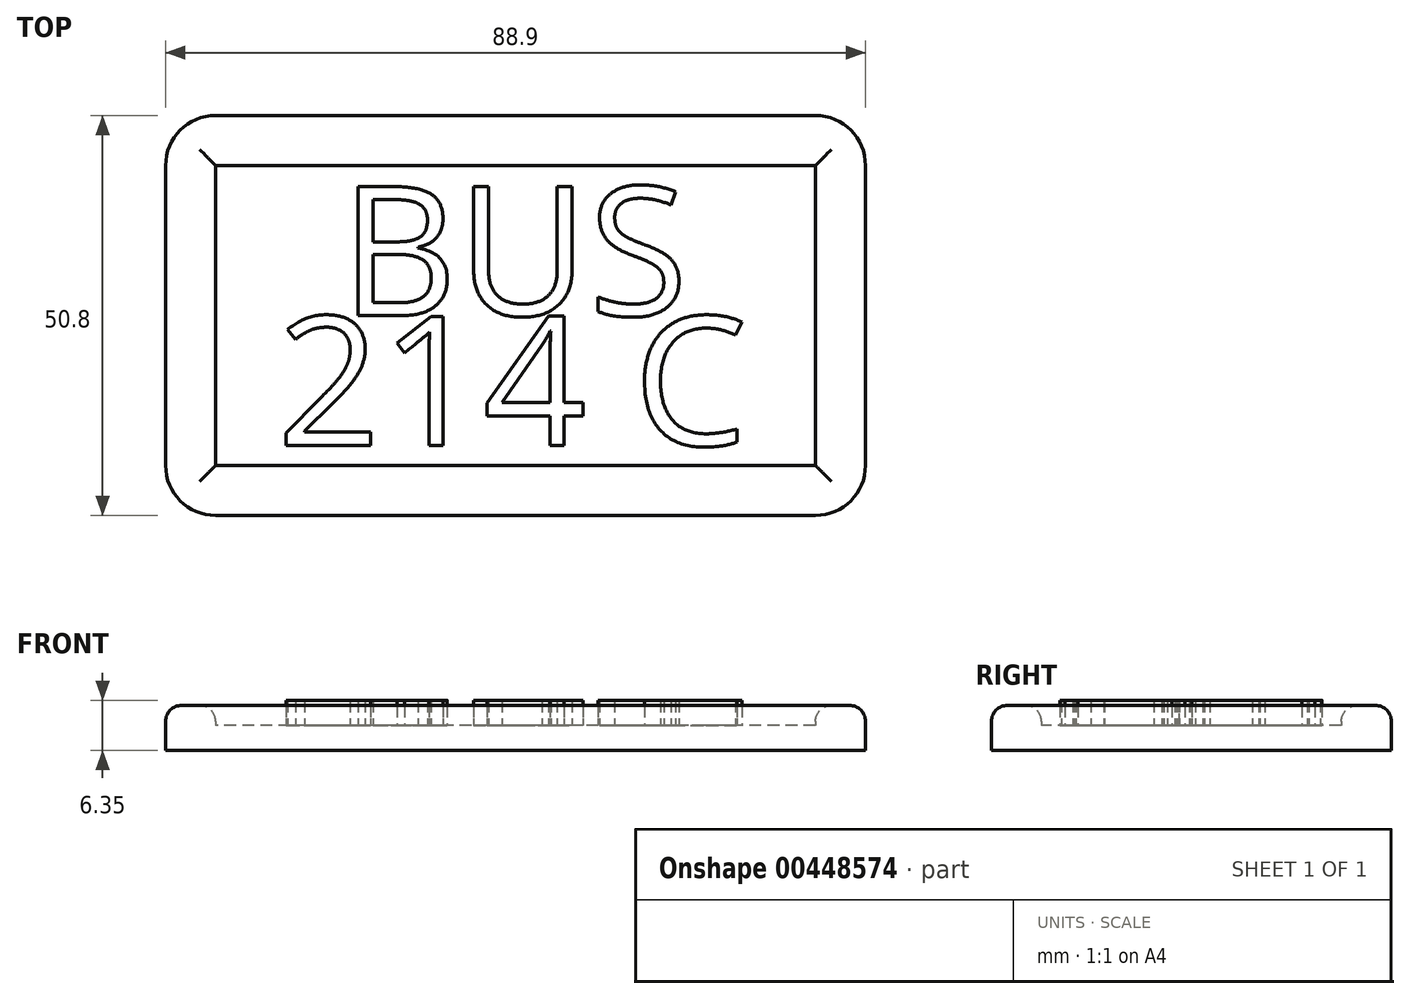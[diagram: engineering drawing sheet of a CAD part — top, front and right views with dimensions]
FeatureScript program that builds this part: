
annotation { "Feature Type Name" : "Feature", "Feature Type Description" : "" }
export const myFeature = defineFeature(function(context is Context, id is Id, definition is map)
    precondition{}
    {
        {
            var Q0;
            Q0=qCreatedBy(makeId("Top.planeOp"),FACE);
            var sketch = newSketch(context, id + "F0", { "sketchPlane" : qUnion([Q0])});
            skLineSegment(sketch, "E0.bottom", {"start": v(38.1, 25.4) * mm, "end": v(-38.1, 25.4) * mm});
            skLineSegment(sketch, "E0.top", {"start": v(38.1, -25.4) * mm, "end": v(-38.1, -25.4) * mm});
            skLineSegment(sketch, "E0.left", {"start": v(44.45, 19.05) * mm, "end": v(44.45, -19.05) * mm});
            skLineSegment(sketch, "E0.right", {"start": v(-44.45, 19.05) * mm, "end": v(-44.45, -19.05) * mm});
            skPoint(sketch, "E0.middle", {"position": v(0, 0) * mm});
            skPoint(sketch, "E1.visualSharp", {"position": v(-44.45, 25.4) * mm});
            skArc(sketch, "E1.filletArc", {"start": v(-38.1, 25.4) * mm, "mid": v(-42.6, 23.54) * mm, "end": v(-44.45, 19.05) * mm});
            skPoint(sketch, "E2.visualSharp", {"position": v(44.45, 25.4) * mm});
            skArc(sketch, "E2.filletArc", {"start": v(44.45, 19.05) * mm, "mid": v(42.6, 23.54) * mm, "end": v(38.1, 25.4) * mm});
            skPoint(sketch, "E3.visualSharp", {"position": v(44.45, -25.4) * mm});
            skArc(sketch, "E3.filletArc", {"start": v(38.1, -25.4) * mm, "mid": v(42.6, -23.54) * mm, "end": v(44.45, -19.05) * mm});
            skPoint(sketch, "E4.visualSharp", {"position": v(-44.45, -25.4) * mm});
            skArc(sketch, "E4.filletArc", {"start": v(-44.45, -19.05) * mm, "mid": v(-42.6, -23.54) * mm, "end": v(-38.1, -25.4) * mm});
            skLineSegment(sketch, "E5.0", {"start": v(38.1, 19.05) * mm, "end": v(38.1, -19.05) * mm});
            skLineSegment(sketch, "E5.1", {"start": v(38.1, -19.05) * mm, "end": v(38.1, -19.05) * mm});
            skLineSegment(sketch, "E5.2", {"start": v(38.1, 19.05) * mm, "end": v(38.1, 19.05) * mm});
            skLineSegment(sketch, "E5.3", {"start": v(38.1, -19.05) * mm, "end": v(-38.1, -19.05) * mm});
            skLineSegment(sketch, "E5.4", {"start": v(38.1, 19.05) * mm, "end": v(-38.1, 19.05) * mm});
            skLineSegment(sketch, "E5.5", {"start": v(-38.1, 19.05) * mm, "end": v(-38.1, 19.05) * mm});
            skLineSegment(sketch, "E5.6", {"start": v(-38.1, 19.05) * mm, "end": v(-38.1, -19.05) * mm});
            skLineSegment(sketch, "E5.7", {"start": v(-38.1, -19.05) * mm, "end": v(-38.1, -19.05) * mm});
            skLineSegment(sketch, "E6.0", {"start": v(44.45, 16.5) * mm, "end": v(-44.45, 16.5) * mm, "construction": true});
            skText(sketch, "E7", { "text": "BUS", "fontName": "OpenSans-Regular.ttf"});
            skLineSegment(sketch, "E8.0", {"start": v(44.45, -16.5) * mm, "end": v(-44.45, -16.5) * mm, "construction": true});
            skText(sketch, "E9", { "text": "214 C", "fontName": "OpenSans-Regular.ttf"});
            const initialGuessF0  = {"E7": [-0.02226, 0, 1, 0, 0.0165], "E9": [-0.03028, -0.0165, 1, 0, 0.0165]};
            skSetInitialGuess(sketch, initialGuessF0);
            skSolve(sketch);
        }
        {
            var Q0;
            Q0=makeQuery(id+"F0.imprint","IMPRINT",FACE,{"disambiguationData":[TD([[makeQuery(id+"F0.imprint","IMPRINT",EDGE,{"derivedFrom":sQuery(id+"F0.wireOp",EDGE,"E0.bottom")}),1.0]])]});
            extrude(context, id + "F1", {"entities" : qUnion([Q0]), "depth" : 5.7 * mm, "offsetDistance" : 25.4 * mm});
        }
        {
            var Q0;
            Q0=makeQuery(id+"F0.imprint","IMPRINT",FACE,{"disambiguationData":[TD([[makeQuery(id+"F0.imprint","IMPRINT",EDGE,{"derivedFrom":sQuery(id+"F0.wireOp",EDGE,"E5.0")}),-1.0]])]});
            extrude(context, id + "F2", {"entities" : qUnion([Q0]), "operationType" : NewBodyOperationType.ADD, "depth" : 3.17 * mm, "offsetDistance" : 25.4 * mm});
        }
        {
            var Q0;
            {var subQ1=sQuery(id+"F0.wireOp",EDGE,"E7.sketch_text.stroke-0");Q0=makeQuery(id+"F0.imprint","IMPRINT",FACE,{"disambiguationData":[TD([[makeQuery(id+"F0.imprint","IMPRINT",EDGE,{"derivedFrom":subQ1}),-1.0]])]});}
            var Q1;
            Q1=makeQuery(id+"F0.imprint","IMPRINT",FACE,{"disambiguationData":[TD([[makeQuery(id+"F0.imprint","IMPRINT",EDGE,{"derivedFrom":sQuery(id+"F0.wireOp",EDGE,"E7.sketch_text.stroke-25")}),-1.0]])]});
            var Q2;
            Q2=makeQuery(id+"F0.imprint","IMPRINT",FACE,{"disambiguationData":[TD([[makeQuery(id+"F0.imprint","IMPRINT",EDGE,{"derivedFrom":sQuery(id+"F0.wireOp",EDGE,"E7.sketch_text.stroke-39")}),-1.0]])]});
            var Q3;
            Q3=makeQuery(id+"F0.imprint","IMPRINT",FACE,{"disambiguationData":[TD([[makeQuery(id+"F0.imprint","IMPRINT",EDGE,{"derivedFrom":sQuery(id+"F0.wireOp",EDGE,"E9.sketch_text.stroke-46")}),-1.0]])]});
            var Q4;
            Q4=makeQuery(id+"F0.imprint","IMPRINT",FACE,{"disambiguationData":[TD([[makeQuery(id+"F0.imprint","IMPRINT",EDGE,{"derivedFrom":sQuery(id+"F0.wireOp",EDGE,"E9.sketch_text.stroke-29")}),-1.0]])]});
            var Q5;
            Q5=makeQuery(id+"F0.imprint","IMPRINT",FACE,{"disambiguationData":[TD([[makeQuery(id+"F0.imprint","IMPRINT",EDGE,{"derivedFrom":sQuery(id+"F0.wireOp",EDGE,"E9.sketch_text.stroke-20")}),-1.0]])]});
            var Q6;
            Q6=makeQuery(id+"F0.imprint","IMPRINT",FACE,{"disambiguationData":[TD([[makeQuery(id+"F0.imprint","IMPRINT",EDGE,{"derivedFrom":sQuery(id+"F0.wireOp",EDGE,"E9.sketch_text.stroke-0")}),-1.0]])]});
            extrude(context, id + "F3", {"entities" : qUnion([Q0, Q1, Q2, Q3, Q4, Q5, Q6]), "operationType" : NewBodyOperationType.ADD, "depth" : 6.35 * mm, "offsetDistance" : 25.4 * mm});
        }
        {
            var Q0;
            Q0=makeQuery(id+"F0.imprint","IMPRINT",FACE,{"disambiguationData":[TD([[makeQuery(id+"F0.imprint","IMPRINT",EDGE,{"derivedFrom":sQuery(id+"F0.wireOp",EDGE,"E9.sketch_text.stroke-40")}),1.0]])]});
            var Q1;
            Q1=makeQuery(id+"F0.imprint","IMPRINT",FACE,{"disambiguationData":[TD([[makeQuery(id+"F0.imprint","IMPRINT",EDGE,{"derivedFrom":sQuery(id+"F0.wireOp",EDGE,"E7.sketch_text.stroke-18")}),1.0]])]});
            var Q2;
            Q2=makeQuery(id+"F0.imprint","IMPRINT",FACE,{"disambiguationData":[TD([[makeQuery(id+"F0.imprint","IMPRINT",EDGE,{"derivedFrom":sQuery(id+"F0.wireOp",EDGE,"E7.sketch_text.stroke-11")}),1.0]])]});
            var Q3;
            Q3=makeQuery(id+"F2.opExtrude","CAP_FACE",FACE,{"disambiguationData":[OSD([sQuery(id+"F0.wireOp",EDGE,"E5.0"),sQuery(id+"F0.wireOp",EDGE,"E5.3"),sQuery(id+"F0.wireOp",EDGE,"E5.4"),sQuery(id+"F0.wireOp",EDGE,"E5.6"),sQuery(id+"F0.wireOp",EDGE,"E7.sketch_text.stroke-0"),sQuery(id+"F0.wireOp",EDGE,"E7.sketch_text.stroke-1"),sQuery(id+"F0.wireOp",EDGE,"E7.sketch_text.stroke-2"),sQuery(id+"F0.wireOp",EDGE,"E7.sketch_text.stroke-3"),sQuery(id+"F0.wireOp",EDGE,"E7.sketch_text.stroke-4"),sQuery(id+"F0.wireOp",EDGE,"E7.sketch_text.stroke-5"),sQuery(id+"F0.wireOp",EDGE,"E7.sketch_text.stroke-6"),sQuery(id+"F0.wireOp",EDGE,"E7.sketch_text.stroke-7"),sQuery(id+"F0.wireOp",EDGE,"E7.sketch_text.stroke-8"),sQuery(id+"F0.wireOp",EDGE,"E7.sketch_text.stroke-9"),sQuery(id+"F0.wireOp",EDGE,"E7.sketch_text.stroke-10"),sQuery(id+"F0.wireOp",EDGE,"E7.sketch_text.stroke-25"),sQuery(id+"F0.wireOp",EDGE,"E7.sketch_text.stroke-26"),sQuery(id+"F0.wireOp",EDGE,"E7.sketch_text.stroke-27"),sQuery(id+"F0.wireOp",EDGE,"E7.sketch_text.stroke-28"),sQuery(id+"F0.wireOp",EDGE,"E7.sketch_text.stroke-29"),sQuery(id+"F0.wireOp",EDGE,"E7.sketch_text.stroke-30"),sQuery(id+"F0.wireOp",EDGE,"E7.sketch_text.stroke-31"),sQuery(id+"F0.wireOp",EDGE,"E7.sketch_text.stroke-32"),sQuery(id+"F0.wireOp",EDGE,"E7.sketch_text.stroke-33"),sQuery(id+"F0.wireOp",EDGE,"E7.sketch_text.stroke-34"),sQuery(id+"F0.wireOp",EDGE,"E7.sketch_text.stroke-35"),sQuery(id+"F0.wireOp",EDGE,"E7.sketch_text.stroke-36"),sQuery(id+"F0.wireOp",EDGE,"E7.sketch_text.stroke-37"),sQuery(id+"F0.wireOp",EDGE,"E7.sketch_text.stroke-38"),sQuery(id+"F0.wireOp",EDGE,"E7.sketch_text.stroke-39"),sQuery(id+"F0.wireOp",EDGE,"E7.sketch_text.stroke-40"),sQuery(id+"F0.wireOp",EDGE,"E7.sketch_text.stroke-41"),sQuery(id+"F0.wireOp",EDGE,"E7.sketch_text.stroke-42"),sQuery(id+"F0.wireOp",EDGE,"E7.sketch_text.stroke-43"),sQuery(id+"F0.wireOp",EDGE,"E7.sketch_text.stroke-44"),sQuery(id+"F0.wireOp",EDGE,"E7.sketch_text.stroke-45"),sQuery(id+"F0.wireOp",EDGE,"E7.sketch_text.stroke-46"),sQuery(id+"F0.wireOp",EDGE,"E7.sketch_text.stroke-47"),sQuery(id+"F0.wireOp",EDGE,"E7.sketch_text.stroke-48"),sQuery(id+"F0.wireOp",EDGE,"E7.sketch_text.stroke-49"),sQuery(id+"F0.wireOp",EDGE,"E7.sketch_text.stroke-50"),sQuery(id+"F0.wireOp",EDGE,"E7.sketch_text.stroke-51"),sQuery(id+"F0.wireOp",EDGE,"E7.sketch_text.stroke-52"),sQuery(id+"F0.wireOp",EDGE,"E7.sketch_text.stroke-53"),sQuery(id+"F0.wireOp",EDGE,"E7.sketch_text.stroke-54"),sQuery(id+"F0.wireOp",EDGE,"E7.sketch_text.stroke-55"),sQuery(id+"F0.wireOp",EDGE,"E7.sketch_text.stroke-56"),sQuery(id+"F0.wireOp",EDGE,"E7.sketch_text.stroke-57"),sQuery(id+"F0.wireOp",EDGE,"E7.sketch_text.stroke-58"),sQuery(id+"F0.wireOp",EDGE,"E7.sketch_text.stroke-59"),sQuery(id+"F0.wireOp",EDGE,"E7.sketch_text.stroke-60"),sQuery(id+"F0.wireOp",EDGE,"E7.sketch_text.stroke-61"),sQuery(id+"F0.wireOp",EDGE,"E7.sketch_text.stroke-62"),sQuery(id+"F0.wireOp",EDGE,"E7.sketch_text.stroke-63"),sQuery(id+"F0.wireOp",EDGE,"E9.sketch_text.stroke-0"),sQuery(id+"F0.wireOp",EDGE,"E9.sketch_text.stroke-1"),sQuery(id+"F0.wireOp",EDGE,"E9.sketch_text.stroke-2"),sQuery(id+"F0.wireOp",EDGE,"E9.sketch_text.stroke-3"),sQuery(id+"F0.wireOp",EDGE,"E9.sketch_text.stroke-4"),sQuery(id+"F0.wireOp",EDGE,"E9.sketch_text.stroke-5"),sQuery(id+"F0.wireOp",EDGE,"E9.sketch_text.stroke-6"),sQuery(id+"F0.wireOp",EDGE,"E9.sketch_text.stroke-7"),sQuery(id+"F0.wireOp",EDGE,"E9.sketch_text.stroke-8"),sQuery(id+"F0.wireOp",EDGE,"E9.sketch_text.stroke-9"),sQuery(id+"F0.wireOp",EDGE,"E9.sketch_text.stroke-10"),sQuery(id+"F0.wireOp",EDGE,"E9.sketch_text.stroke-11"),sQuery(id+"F0.wireOp",EDGE,"E9.sketch_text.stroke-12"),sQuery(id+"F0.wireOp",EDGE,"E9.sketch_text.stroke-13"),sQuery(id+"F0.wireOp",EDGE,"E9.sketch_text.stroke-14"),sQuery(id+"F0.wireOp",EDGE,"E9.sketch_text.stroke-15"),sQuery(id+"F0.wireOp",EDGE,"E9.sketch_text.stroke-16"),sQuery(id+"F0.wireOp",EDGE,"E9.sketch_text.stroke-17"),sQuery(id+"F0.wireOp",EDGE,"E9.sketch_text.stroke-18"),sQuery(id+"F0.wireOp",EDGE,"E9.sketch_text.stroke-19"),sQuery(id+"F0.wireOp",EDGE,"E9.sketch_text.stroke-20"),sQuery(id+"F0.wireOp",EDGE,"E9.sketch_text.stroke-21"),sQuery(id+"F0.wireOp",EDGE,"E9.sketch_text.stroke-22"),sQuery(id+"F0.wireOp",EDGE,"E9.sketch_text.stroke-23"),sQuery(id+"F0.wireOp",EDGE,"E9.sketch_text.stroke-24"),sQuery(id+"F0.wireOp",EDGE,"E9.sketch_text.stroke-25"),sQuery(id+"F0.wireOp",EDGE,"E9.sketch_text.stroke-26"),sQuery(id+"F0.wireOp",EDGE,"E9.sketch_text.stroke-27"),sQuery(id+"F0.wireOp",EDGE,"E9.sketch_text.stroke-28"),sQuery(id+"F0.wireOp",EDGE,"E9.sketch_text.stroke-29"),sQuery(id+"F0.wireOp",EDGE,"E9.sketch_text.stroke-30"),sQuery(id+"F0.wireOp",EDGE,"E9.sketch_text.stroke-31"),sQuery(id+"F0.wireOp",EDGE,"E9.sketch_text.stroke-32"),sQuery(id+"F0.wireOp",EDGE,"E9.sketch_text.stroke-33"),sQuery(id+"F0.wireOp",EDGE,"E9.sketch_text.stroke-34"),sQuery(id+"F0.wireOp",EDGE,"E9.sketch_text.stroke-35"),sQuery(id+"F0.wireOp",EDGE,"E9.sketch_text.stroke-36"),sQuery(id+"F0.wireOp",EDGE,"E9.sketch_text.stroke-37"),sQuery(id+"F0.wireOp",EDGE,"E9.sketch_text.stroke-38"),sQuery(id+"F0.wireOp",EDGE,"E9.sketch_text.stroke-39"),sQuery(id+"F0.wireOp",EDGE,"E9.sketch_text.stroke-46"),sQuery(id+"F0.wireOp",EDGE,"E9.sketch_text.stroke-47"),sQuery(id+"F0.wireOp",EDGE,"E9.sketch_text.stroke-48"),sQuery(id+"F0.wireOp",EDGE,"E9.sketch_text.stroke-49"),sQuery(id+"F0.wireOp",EDGE,"E9.sketch_text.stroke-50"),sQuery(id+"F0.wireOp",EDGE,"E9.sketch_text.stroke-51"),sQuery(id+"F0.wireOp",EDGE,"E9.sketch_text.stroke-52"),sQuery(id+"F0.wireOp",EDGE,"E9.sketch_text.stroke-53"),sQuery(id+"F0.wireOp",EDGE,"E9.sketch_text.stroke-54"),sQuery(id+"F0.wireOp",EDGE,"E9.sketch_text.stroke-55"),sQuery(id+"F0.wireOp",EDGE,"E9.sketch_text.stroke-56"),sQuery(id+"F0.wireOp",EDGE,"E9.sketch_text.stroke-57"),sQuery(id+"F0.wireOp",EDGE,"E9.sketch_text.stroke-58"),sQuery(id+"F0.wireOp",EDGE,"E9.sketch_text.stroke-59"),sQuery(id+"F0.wireOp",EDGE,"E9.sketch_text.stroke-60")])],"isStart":false});
            extrude(context, id + "F4", {"entities" : qUnion([Q0, Q1, Q2]), "operationType" : NewBodyOperationType.ADD, "endBound" : BoundingType.UP_TO_SURFACE, "depth" : 25.4 * mm, "endBoundEntityFace" : qUnion([Q3]), "offsetDistance" : 25.4 * mm});
        }
        {
            var Q0;
            Q0=makeQuery(id+"F1.opExtrude","CAP_EDGE",EDGE,{"disambiguationData":[OSD([sQuery(id+"F0.wireOp",EDGE,"E0.top")])],"isStart":false});
            var Q1;
            Q1=makeQuery(id+"F1.opExtrude","CAP_EDGE",EDGE,{"disambiguationData":[OSD([sQuery(id+"F0.wireOp",EDGE,"E5.4")])],"isStart":false});
            var Q2;
            Q2=makeQuery(id+"F1.opExtrude","CAP_EDGE",EDGE,{"disambiguationData":[OSD([sQuery(id+"F0.wireOp",EDGE,"E5.0")])],"isStart":false});
            var Q3;
            Q3=makeQuery(id+"F1.opExtrude","CAP_EDGE",EDGE,{"disambiguationData":[OSD([sQuery(id+"F0.wireOp",EDGE,"E5.3")])],"isStart":false});
            var Q4;
            Q4=makeQuery(id+"F1.opExtrude","CAP_EDGE",EDGE,{"disambiguationData":[OSD([sQuery(id+"F0.wireOp",EDGE,"E5.6")])],"isStart":false});
            fillet(context, id + "F5", {"entities" : qUnion([Q0, Q1, Q2, Q3, Q4]), "radius" : 2.03 * mm, "tangentPropagation" : true, "allowEdgeOverflow" : false});
        }
    });
